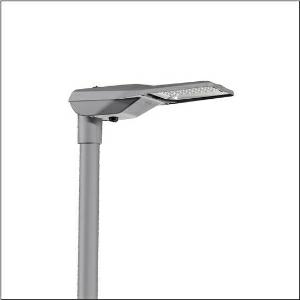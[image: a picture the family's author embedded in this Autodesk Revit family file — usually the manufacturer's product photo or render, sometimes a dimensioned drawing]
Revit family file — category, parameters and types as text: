
# Revit family: streetlight_sl_21_mini___stw1_0a_5xe2e43t08gb_b683
name_source: partatom
category: Lighting Fixtures
units: mm (PartAtom-declared; Revit-internal decimal feet)

## family parameters
Cut with Voids When Loaded = No
Host = Face
Light Source = No
Part Type = Normal
Room Calculation Point = No
Round Connector Dimension = Use Diameter
Shared = No

## types (1)
- --- (1 x LED, 6180 lm, 40.4 W, 4000K)
    Apparent Load = 40 VA
    CIE Flux Codes = 38 75 98 100 100
    Color Rendering = 70
    Color Temperature = 4000K
    Default Elevation = 1800 mm
    Description = Streetlight SL 21 mini, mast luminaire, primary light control with lens, of PMMA, primary optical cover: cover, of toughened safety glass, transparent, light distribution: STW1.0a, light emission: direct distribution, primary light characteristic: asymmetric, installation type: side-entry, post-top, LED, High Power LED, rated luminous flux: 6.180lm, luminous efficacy: 153lm/W, light colour: 740, colour temperature: 4000K, control gear: D4i, control: overheat protection, constant luminous flux control, time-dependent luminous flux control, flexible luminous flux parameterisation, pre-setting: logarithmic dimming characteristic, mains connection: 220..240V, AC, 50/60Hz, start of lifetime: 40W, end of service life: 41W, reduction: 19W, luminaire housing, of diecast aluminium, powder-coated, Siteco® metallic grey (DB 702S), corrosivity category C5 mid according to DIN EN ISO 12944, please order mast flange separately, inclination adjustable: 0°, 5°, 10°, 15°, sealing non-destructively replaceable, multi-level sealing system, length: 628mm, width: 235mm, height: 110mm, mast flange for spigot size: 42mm (side-entry): 5XC10008XM4, 60/48mm (side-entry/post-top): 5XC10108XM2, 76/60mm (side-entry/post-top): 5XC10108XM1, mounting height: 4..8m, Smart Interface below and above, protection rating (complete): IP66, insulation class (complete): insulation class II (safety insulation), certification: CE, ENEC, ENEC+, VDE, impact resistance: IK10, permissible operating ambient temperature for outdoor applications: -40..+50°C, standard-compliant lighting for roads and squares, packaging unit: 1 piece

Light Distribution: STW1.0a
    Height = 110 mm
    Lamp = 1 x LED
    Lamp Light Flux = 6180 lm
    Lamp Power = 40.4 W
    Lamp count = 1
    Length = 625 mm
    Luminous efficacy = 153 lm/W
    Manufacturer = Siteco
    ModVariant = No
    Model = 5XE2E43T08GB
    Number of Poles = 1
    OnlyDefault = Yes
    Power Factor = 1
    Product Name = Streetlight SL 21 mini | STW1.0a
    Product group = mast luminaire | pylon top
    ProductGroupID = 6100
    Protection Class = Protection class II
    Protection Degree = IP 66
    RLX_Detail_Level = 1
    RLX_Emergency_Light_Flux = 0 lm
    RLX_Emergency_Type = 0
    RLX_Emergency_Type_DB = No
    RlxData = <blob elided: 26357 chars, md5=4af80c03>
    Socket = socket
    Standby Power = 0 W
    System Light Flux = 6180 lm
    System Power = 40 W
    Type Comments = factory setting: luminous flux: 100 % | dim-lin: 254 | 812 mA
    Type Image = l_1003514.jpg
    URL = http://relux.com
    VarID = @adj_208559
    Voltage = 0 V
    Weight = 0.00 kg
    Width = 234 mm

## geometry (parser evidence)
native form markers: Blend x4, Sweep x13
no freeform markers — native parametric forms only
